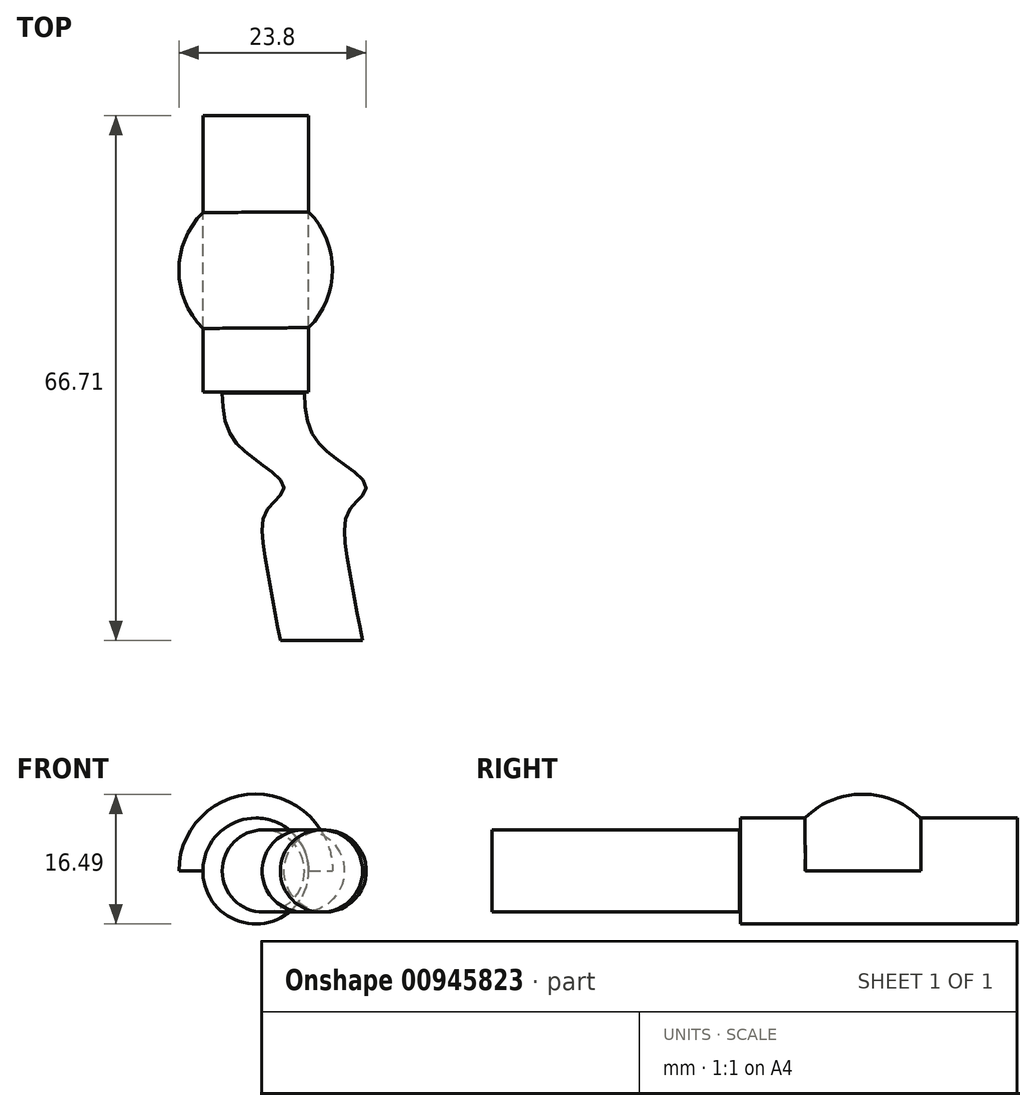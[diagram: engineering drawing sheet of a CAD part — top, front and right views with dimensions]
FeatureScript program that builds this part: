
annotation { "Feature Type Name" : "Feature", "Feature Type Description" : "" }
export const myFeature = defineFeature(function(context is Context, id is Id, definition is map)
    precondition{}
    {
        {
            var Q0;
            Q0=qCreatedBy(makeId("Top.planeOp"),FACE);
            var sketch = newSketch(context, id + "F0", { "sketchPlane" : qUnion([Q0])});
            skArc(sketch, "E0", {"start": v(-101.16, 11.66) * mm, "mid": v(-90.75, 21.42) * mm, "end": v(-99.82, 32.44) * mm});
            skLineSegment(sketch, "E1", {"start": v(-99.82, 32.44) * mm, "end": v(-101.16, 11.66) * mm});
            skSolve(sketch);
        }
        {
            var Q0;
            Q0=makeQuery(id+"F0.imprint","IMPRINT",FACE,{"disambiguationData":[TD([[makeQuery(id+"F0.imprint","IMPRINT",EDGE,{"derivedFrom":sQuery(id+"F0.wireOp",EDGE,"E0")}),1.0]])]});
            var Q1;
            Q1=sQuery(id+"F0.wireOp",EDGE,"E1");
            revolve(context, id + "F1", {"surfaceOperationType" : NewSurfaceOperationType.NEW, "entities" : qUnion([Q0]), "axis" : qUnion([Q1]), "revolveType" : RevolveType.ONE_DIRECTION, "angle" : 180 * degree});
        }
        {
            var Q0;
            Q0=qCreatedBy(makeId("Top.planeOp"),FACE);
            var sketch = newSketch(context, id + "F2", { "sketchPlane" : qUnion([Q0])});
            skLineSegment(sketch, "E2.bottom", {"start": v(-100.49, 41.7) * mm, "end": v(-93.76, 41.7) * mm});
            skLineSegment(sketch, "E2.top", {"start": v(-100.49, 6.54) * mm, "end": v(-93.76, 6.54) * mm});
            skLineSegment(sketch, "E2.left", {"start": v(-100.49, 41.7) * mm, "end": v(-100.49, 6.54) * mm});
            skLineSegment(sketch, "E2.right", {"start": v(-93.76, 41.7) * mm, "end": v(-93.76, 6.54) * mm});
            skSolve(sketch);
        }
        {
            var Q0;
            Q0=makeQuery(id+"F2.imprint","IMPRINT",FACE,{"disambiguationData":[TD([[makeQuery(id+"F2.imprint","IMPRINT",EDGE,{"derivedFrom":sQuery(id+"F2.wireOp",EDGE,"E2.bottom")}),-1.0]])]});
            var Q1;
            Q1=sQuery(id+"F2.wireOp",EDGE,"E2.left");
            revolve(context, id + "F3", {"operationType" : NewBodyOperationType.ADD, "surfaceOperationType" : NewSurfaceOperationType.NEW, "entities" : qUnion([Q0]), "axis" : qUnion([Q1]), "revolveType" : RevolveType.FULL});
        }
        {
            var Q0;
            Q0=makeQuery(id+"F3.opRevolve","SWEPT_FACE",FACE,{"disambiguationData":[OSD([sQuery(id+"F2.wireOp",EDGE,"E2.top")])]});
            cPlane(context, id + "F4", {"entities" : qUnion([Q0]), "cplaneType" : CPlaneType.OFFSET, "offset" : 0.25 * mm, "width" : 152.4 * mm, "height" : 152.4 * mm});
        }
        {
            var Q0;
            Q0=qCreatedBy(id+"F4.planeOp",FACE);
            var sketch = newSketch(context, id + "F5", { "sketchPlane" : qUnion([Q0])});
            skCircle(sketch, "E3", {"center": v(-99.53, 0) * mm, "radius": 5.22 * mm});
            skSolve(sketch);
        }
        {
            var Q0;
            Q0=qCreatedBy(makeId("Top.planeOp"),FACE);
            var sketch = newSketch(context, id + "F6", { "sketchPlane" : qUnion([Q0])});
            skFitSpline(sketch, "E4", {"points": [v(-100.11, 6.41) * mm, v(-98.23, 0) * mm, v(-92.26, -5.4) * mm, v(-94.4, -8.42) * mm, v(-94.66, -14.46) * mm, v(-92.72, -25.02) * mm], "startDerivative": vector(1.26, -33.86) * mm, "endDerivative": vector(8.4, -44.13) * mm});
            skSolve(sketch);
        }
        {
            var Q0;
            Q0=makeQuery(id+"F5.imprint","IMPRINT",FACE,{"disambiguationData":[TD([[makeQuery(id+"F5.imprint","IMPRINT",EDGE,{"derivedFrom":sQuery(id+"F5.wireOp",EDGE,"E3")}),1.0]])]});
            var Q1;
            Q1=sQuery(id+"F6.wireOp",EDGE,"E4");
            sweep(context, id + "F7", {"profiles" : qUnion([Q0]), "path" : qUnion([Q1]), "keepProfileOrientation" : true});
        }
    });
